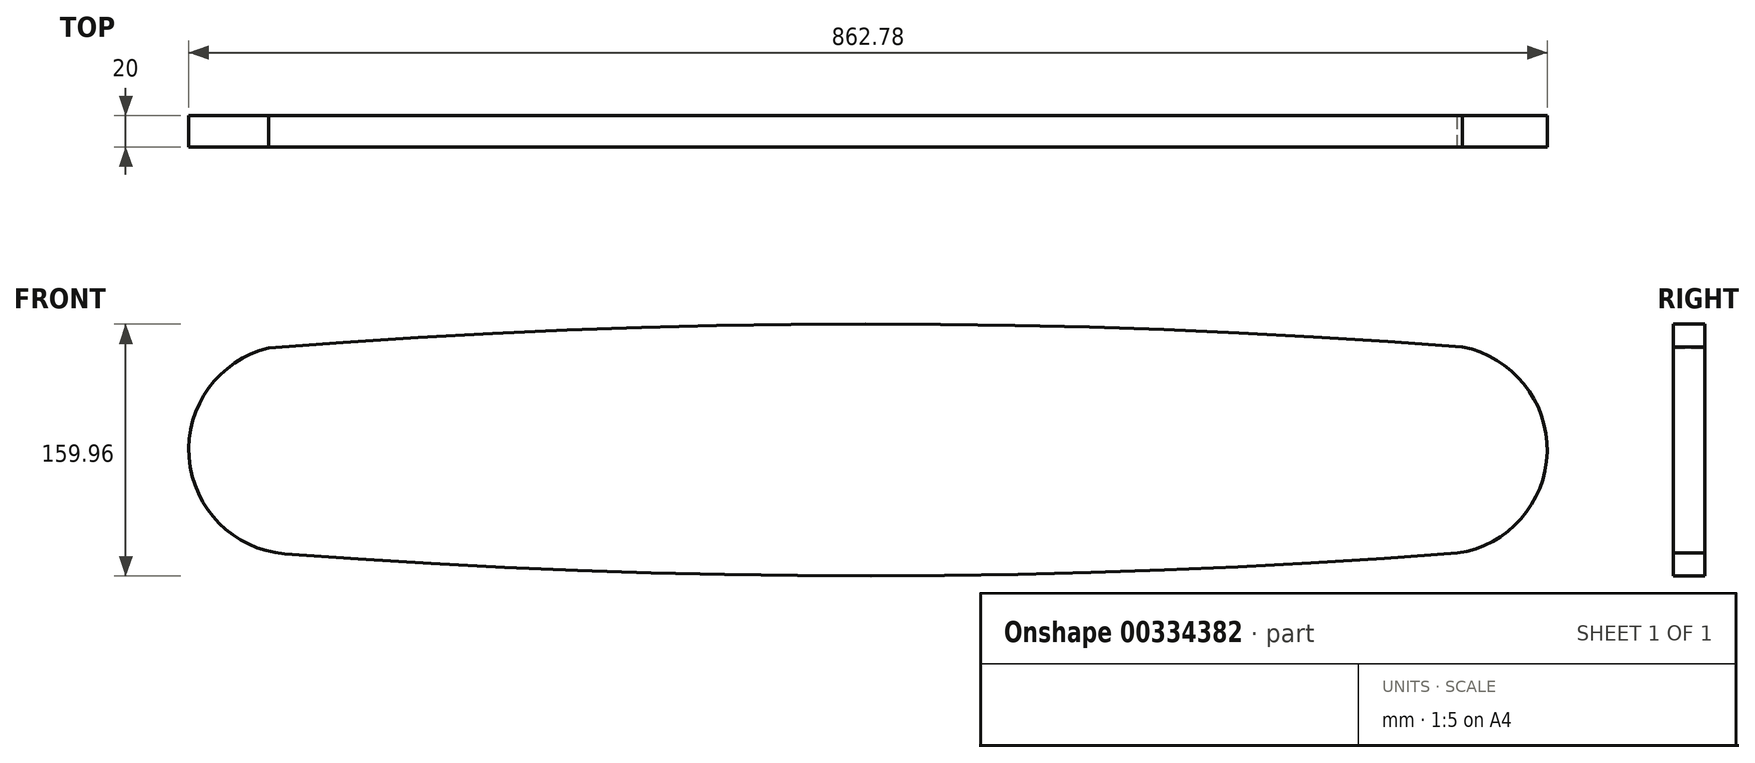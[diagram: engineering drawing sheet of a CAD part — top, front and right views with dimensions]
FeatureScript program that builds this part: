
annotation { "Feature Type Name" : "Feature", "Feature Type Description" : "" }
export const myFeature = defineFeature(function(context is Context, id is Id, definition is map)
    precondition{}
    {
        {
            var Q0;
            Q0=qCreatedBy(makeId("Front.planeOp"),FACE);
            var sketch = newSketch(context, id + "F0", { "sketchPlane" : qUnion([Q0])});
            skCircle(sketch, "E0", {"center": v(-56.8, 0) * mm, "radius": 66.39 * mm});
            skCircle(sketch, "E1", {"center": v(673.2, 0) * mm, "radius": 66.39 * mm});
            skLineSegment(sketch, "E2", {"start": v(-56.8, 0) * mm, "end": v(673.2, 0) * mm});
            skArc(sketch, "E3", {"start": v(-62.27, -66.16) * mm, "mid": v(310.2, -80.26) * mm, "end": v(682.66, -65.71) * mm});
            skArc(sketch, "E4", {"start": v(685.77, 65.19) * mm, "mid": v(306.68, 79.7) * mm, "end": v(-72.38, 64.53) * mm});
            skSolve(sketch);
        }
        {
            var Q0;
            {var subQ0=sQuery(id+"F0.wireOp",EDGE,"E4");var subQ1=sQuery(id+"F0.wireOp",EDGE,"E0");var subQ2=makeQuery(id+"F0.imprint","INTERSECT",VERTEX,{"disambiguationData":[OD(1.0)],"derivedFrom":[subQ1,subQ0]});Q0=makeQuery(id+"F0.imprint","IMPRINT",FACE,{"disambiguationData":[TD([[makeQuery(id+"F0.imprint","IMPRINT",EDGE,{"disambiguationData":[TD([[subQ2,1.0]])],"derivedFrom":subQ1}),-1.0]])]});}
            var Q1;
            {var subQ0=sQuery(id+"F0.wireOp",EDGE,"E2");var subQ1=sQuery(id+"F0.wireOp",EDGE,"E0");var subQ2=makeQuery(id+"F0.imprint","INTERSECT",VERTEX,{"derivedFrom":[subQ1,subQ0]});Q1=makeQuery(id+"F0.imprint","IMPRINT",FACE,{"disambiguationData":[TD([[makeQuery(id+"F0.imprint","IMPRINT",EDGE,{"disambiguationData":[TD([[subQ2,1.0]])],"derivedFrom":subQ1}),-1.0]])]});}
            var Q2;
            {var subQ1=sQuery(id+"F0.wireOp",EDGE,"E0");var subQ4=sQuery(id+"F0.wireOp",EDGE,"E4");var subQ5=makeQuery(id+"F0.imprint","INTERSECT",VERTEX,{"disambiguationData":[OD(1.0)],"derivedFrom":[subQ1,subQ4]});Q2=makeQuery(id+"F0.imprint","IMPRINT",FACE,{"disambiguationData":[TD([[makeQuery(id+"F0.imprint","IMPRINT",EDGE,{"disambiguationData":[TD([[subQ5,1.0]])],"derivedFrom":subQ1}),1.0]])]});}
            var Q3;
            {var subQ1=sQuery(id+"F0.wireOp",EDGE,"E1");var subQ4=sQuery(id+"F0.wireOp",EDGE,"E4");var subQ7=makeQuery(id+"F0.imprint","INTERSECT",VERTEX,{"disambiguationData":[OD(1.0)],"derivedFrom":[subQ1,subQ4]});Q3=makeQuery(id+"F0.imprint","IMPRINT",FACE,{"disambiguationData":[TD([[makeQuery(id+"F0.imprint","IMPRINT",EDGE,{"disambiguationData":[TD([[subQ7,-1.0]])],"derivedFrom":subQ1}),1.0]])]});}
            extrude(context, id + "F1", {"entities" : qUnion([Q0, Q1, Q2, Q3]), "depth" : 20 * mm});
        }
    });
